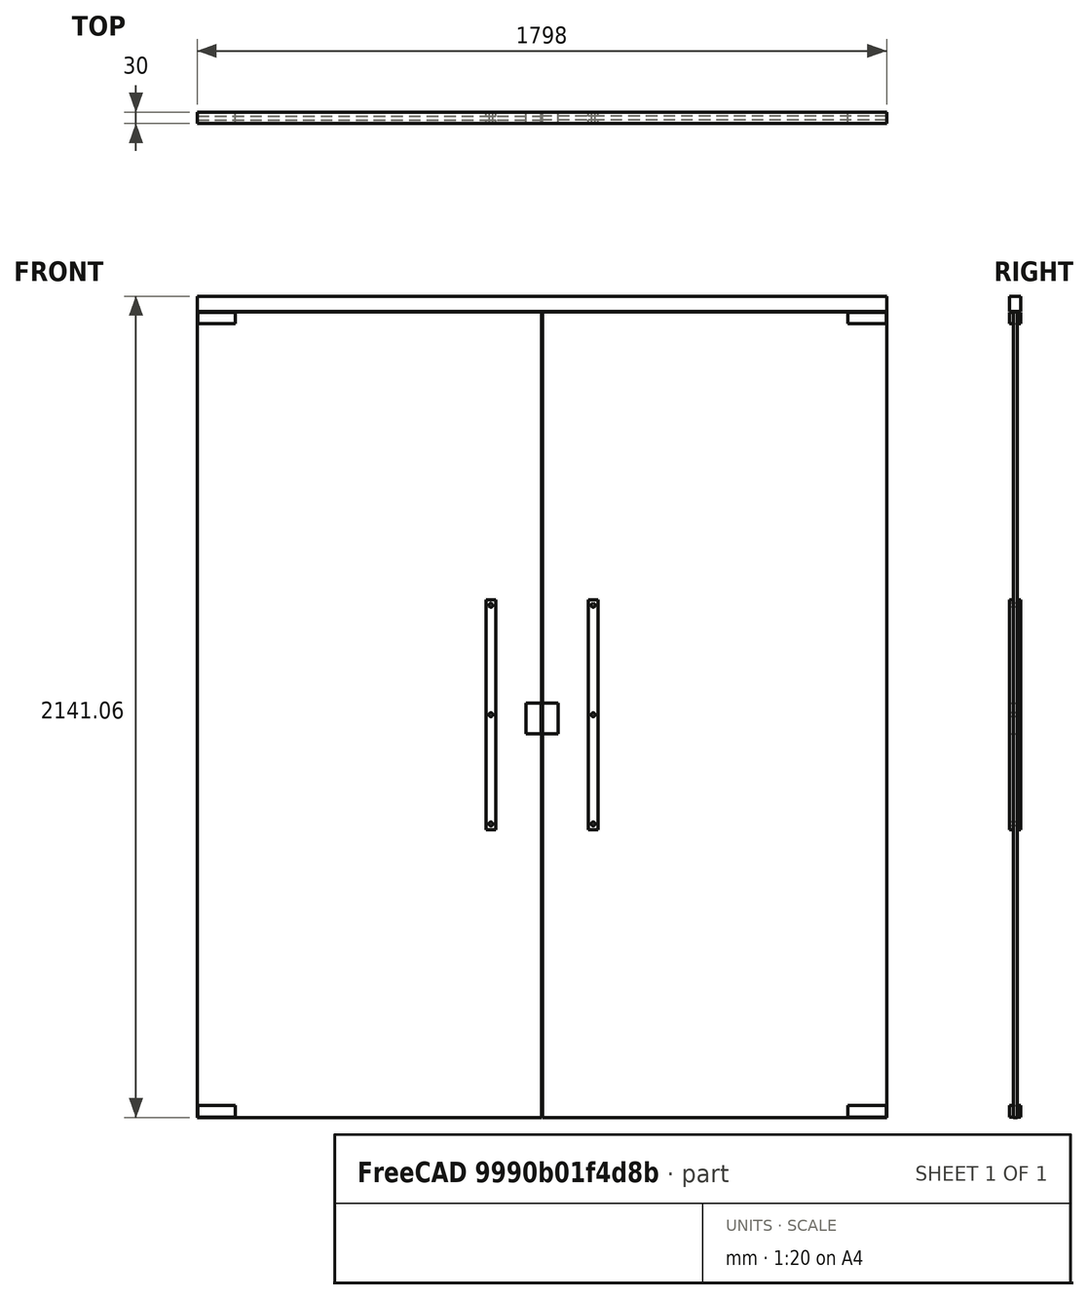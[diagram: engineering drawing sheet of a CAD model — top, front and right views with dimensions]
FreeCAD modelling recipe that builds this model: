
FCSTD DOCUMENT  (FreeCAD 0.16R6704 (Git))
Label: Double glass doors with lintel and handles
License: CreativeCommons Attribution
LicenseURL: http://creativecommons.org/licenses/by/4.0/
objects: Sketcher::SketchObject×3, Part::FeaturePython×1, App::DocumentObjectGroup×1
note: 4 computed .brp shape members not serialized (recipe doc carries the construction recipe); baked Part::Feature solids carry a one-line shape summary decoded from their .brp

FEATURE [Sketcher::SketchObject] Sketch135
  Placement = pos=(0,0,0) rot=(1,0,0;1.5708rad)
  sketch-geometry (63):
    g0: LineSegment StartX=0 StartY=0 StartZ=0 EndX=1800 EndY=0 EndZ=0
    g1: LineSegment StartX=1800 StartY=0 StartZ=0 EndX=1800 EndY=2142 EndZ=0
    g2: LineSegment StartX=1800 StartY=2142 StartZ=0 EndX=0 EndY=2142 EndZ=0
    g3: LineSegment StartX=0 StartY=2142 StartZ=0 EndX=0 EndY=0 EndZ=0
    g4: LineSegment StartX=1 StartY=0 StartZ=0 EndX=899 EndY=0 EndZ=0
    g5: LineSegment StartX=899 StartY=0 StartZ=0 EndX=899 EndY=2100 EndZ=0
    g6: LineSegment StartX=899 StartY=2100 StartZ=0 EndX=1 EndY=2100 EndZ=0
    g7: LineSegment StartX=1 StartY=2100 StartZ=0 EndX=1 EndY=0 EndZ=0
    g8: LineSegment StartX=2 StartY=2099 StartZ=0 EndX=100 EndY=2099 EndZ=0
    g9: LineSegment StartX=100 StartY=2099 StartZ=0 EndX=100 EndY=2069 EndZ=0
    g10: LineSegment StartX=100 StartY=2069 StartZ=0 EndX=2 EndY=2069 EndZ=0
    g11: LineSegment StartX=2 StartY=2069 StartZ=0 EndX=2 EndY=2099 EndZ=0
    g12: LineSegment StartX=2 StartY=1 StartZ=0 EndX=100 EndY=1 EndZ=0
    g13: LineSegment StartX=100 StartY=1 StartZ=0 EndX=100 EndY=31 EndZ=0
    g14: LineSegment StartX=100 StartY=31 StartZ=0 EndX=2 EndY=31 EndZ=0
    g15: LineSegment StartX=2 StartY=31 StartZ=0 EndX=2 EndY=1 EndZ=0
    g16: LineSegment StartX=858 StartY=1080 StartZ=0 EndX=898 EndY=1080 EndZ=0
    g17: LineSegment StartX=898 StartY=1080 StartZ=0 EndX=898 EndY=1000 EndZ=0
    g18: LineSegment StartX=898 StartY=1000 StartZ=0 EndX=858 EndY=1000 EndZ=0
    g19: LineSegment StartX=858 StartY=1000 StartZ=0 EndX=858 EndY=1080 EndZ=0
    g20: LineSegment StartX=754 StartY=1350 StartZ=0 EndX=779 EndY=1350 EndZ=0
    g21: LineSegment StartX=779 StartY=1350 StartZ=0 EndX=779 EndY=750 EndZ=0
    g22: LineSegment StartX=779 StartY=750 StartZ=0 EndX=754 EndY=750 EndZ=0
    g23: LineSegment StartX=754 StartY=750 StartZ=0 EndX=754 EndY=1350 EndZ=0
    g24: LineSegment [constr] StartX=766.5 StartY=1477.64 StartZ=0 EndX=766.5 EndY=711 EndZ=0
    g25: Circle CenterX=766.5 CenterY=1335 CenterZ=0 NormalX=0 NormalY=0 NormalZ=1 Radius=5
    g26: Circle CenterX=766.5 CenterY=1050 CenterZ=0 NormalX=0 NormalY=0 NormalZ=1 Radius=5
    g27: Circle CenterX=766.5 CenterY=765 CenterZ=0 NormalX=0 NormalY=0 NormalZ=1 Radius=5
    g28: LineSegment [constr] StartX=712 StartY=1050 StartZ=0 EndX=790 EndY=1050 EndZ=0
    g29: LineSegment [constr] StartX=900 StartY=2725.36 StartZ=0 EndX=900 EndY=-391.189 EndZ=0
    g30: LineSegment StartX=1799 StartY=-0.0580396 StartZ=0 EndX=901 EndY=-0.0580396 EndZ=0
    g31: LineSegment StartX=901 StartY=-0.0580396 StartZ=0 EndX=901 EndY=2100 EndZ=0
    g32: LineSegment StartX=901 StartY=2100 StartZ=0 EndX=1799 EndY=2100 EndZ=0
    g33: LineSegment StartX=1799 StartY=2100 StartZ=0 EndX=1799 EndY=-0.0580396 EndZ=0
    g34: LineSegment StartX=1798 StartY=2099 StartZ=0 EndX=1698 EndY=2099 EndZ=0
    g35: LineSegment StartX=1698 StartY=2099 StartZ=0 EndX=1698 EndY=2068.94 EndZ=0
    g36: LineSegment StartX=1698 StartY=2068.94 StartZ=0 EndX=1798 EndY=2068.94 EndZ=0
    g37: LineSegment StartX=1798 StartY=2068.94 StartZ=0 EndX=1798 EndY=2099 EndZ=0
    g38: LineSegment StartX=1798 StartY=0.94196 StartZ=0 EndX=1698 EndY=0.94196 EndZ=0
    g39: LineSegment StartX=1698 StartY=0.94196 StartZ=0 EndX=1698 EndY=31.0014 EndZ=0
    g40: LineSegment StartX=1698 StartY=31.0014 StartZ=0 EndX=1798 EndY=31.0014 EndZ=0
    g41: LineSegment StartX=1798 StartY=31.0014 StartZ=0 EndX=1798 EndY=0.94196 EndZ=0
    g42: LineSegment StartX=942 StartY=1080 StartZ=0 EndX=902 EndY=1080 EndZ=0
    g43: LineSegment StartX=902 StartY=1080 StartZ=0 EndX=902 EndY=1000 EndZ=0
    g44: LineSegment StartX=902 StartY=1000 StartZ=0 EndX=942 EndY=1000 EndZ=0
    g45: LineSegment StartX=942 StartY=1000 StartZ=0 EndX=942 EndY=1080 EndZ=0
    g46: LineSegment StartX=1046 StartY=1350 StartZ=0 EndX=1021 EndY=1350 EndZ=0
    g47: LineSegment StartX=1021 StartY=1350 StartZ=0 EndX=1021 EndY=750 EndZ=0
    g48: LineSegment StartX=1021 StartY=750 StartZ=0 EndX=1046 EndY=750 EndZ=0
    g49: LineSegment StartX=1046 StartY=750 StartZ=0 EndX=1046 EndY=1350 EndZ=0
    g50: LineSegment [constr] StartX=1033.5 StartY=1477.64 StartZ=0 EndX=1033.5 EndY=711 EndZ=0
    g51: Circle CenterX=1033.5 CenterY=1335 CenterZ=0 NormalX=0 NormalY=0 NormalZ=1 Radius=5
    g52: Circle CenterX=1033.5 CenterY=1050 CenterZ=0 NormalX=0 NormalY=0 NormalZ=1 Radius=5
    g53: Circle CenterX=1033.5 CenterY=765 CenterZ=0 NormalX=0 NormalY=0 NormalZ=1 Radius=5
    g54: LineSegment [constr] StartX=1088 StartY=1050 StartZ=0 EndX=1010 EndY=1050 EndZ=0
    g55: LineSegment StartX=-1 StartY=2143 StartZ=0 EndX=1801 EndY=2143 EndZ=0
    g56: LineSegment StartX=1801 StartY=2143 StartZ=0 EndX=1801 EndY=0 EndZ=0
    g57: LineSegment StartX=1801 StartY=0 StartZ=0 EndX=-1 EndY=0 EndZ=0
    g58: LineSegment StartX=-1 StartY=0 StartZ=0 EndX=-1 EndY=2143 EndZ=0
    g59: LineSegment StartX=1 StartY=2141 StartZ=0 EndX=1799 EndY=2141 EndZ=0
    g60: LineSegment StartX=1799 StartY=2141 StartZ=0 EndX=1799 EndY=2101 EndZ=0
    g61: LineSegment StartX=1799 StartY=2101 StartZ=0 EndX=1 EndY=2101 EndZ=0
    g62: LineSegment StartX=1 StartY=2101 StartZ=0 EndX=1 EndY=2141 EndZ=0
  constraints (177):
    c: Coincident(g0,g1)
    c: Coincident(g1,g2)
    c: Coincident(g2,g3)
    c: Coincident(g3,g0)
    c: Horizontal(g0)
    c: Horizontal(g2)
    c: Vertical(g1)
    c: Vertical(g3)
    c: Coincident(g4,g5)
    c: Coincident(g5,g6)
    c: Coincident(g6,g7)
    c: Coincident(g7,g4)
    c: Horizontal(g4)
    c: Horizontal(g6)
    c: Vertical(g5)
    c: Vertical(g7)
    c: DistanceX(g0) = 1800  'Largura vão'
    c: DistanceX(g2,g6) = 1  'Constraint18'
    c: DistanceY(g0,g4) = 0
    c: Coincident(g0,g-1)
    c: Coincident(g8,g9)
    c: Coincident(g9,g10)
    c: Coincident(g10,g11)
    c: Coincident(g11,g8)
    c: Horizontal(g8)
    c: Horizontal(g10)
    c: Vertical(g9)
    c: Vertical(g11)
    c: Coincident(g12,g13)
    c: Coincident(g13,g14)
    c: Coincident(g14,g15)
    c: Coincident(g15,g12)
    c: Horizontal(g12)
    c: Horizontal(g14)
    c: Vertical(g13)
    c: Vertical(g15)
    c: Coincident(g16,g17)
    c: Coincident(g17,g18)
    c: Coincident(g18,g19)
    c: Coincident(g19,g16)
    c: Horizontal(g16)
    c: Horizontal(g18)
    c: Vertical(g17)
    c: Vertical(g19)
    c: DistanceY(g8,g6) = 1
    c: DistanceX(g6,g8) = 1
    c: DistanceY(g9,g8) = 30  'Altura apoio'
    c: DistanceX(g10,g9) = 98  'Largura apoio'
    c: Equal(g9,g13)
    c: Equal(g14,g8)
    c: DistanceX(g4,g12) = 1
    c: DistanceY(g4,g12) = 1
    c: DistanceX(g17,g4) = 1
    c: DistanceY(g18,g16) = 80  'Altura tranca'
    c: DistanceX(g16,g16) = 40  'Largura tranca'
    c: DistanceY(g4,g18) = 1000  'Altura da tranca ao chão'
    c: Coincident(g20,g21)
    c: Coincident(g21,g22)
    c: Coincident(g22,g23)
    c: Coincident(g23,g20)
    c: Horizontal(g20)
    c: Horizontal(g22)
    c: Vertical(g21)
    c: Vertical(g23)
    c: DistanceX(g20,g20) = 25  'Largura puxador'
    c: DistanceY(g21,g20) = 600  'Altura do puxador'
    c: Vertical(g24)  'Constraint69'
    c: Symmetric(g20,g20,g24)
    c: PointOnObject(g25,g24)  'Constraint72'
    c: PointOnObject(g26,g24)  'Constraint71'
    c: PointOnObject(g27,g24)
    c: Radius(g27) = 5  'Apoio puxador'
    c: Equal(g27,g26)  'Constraint83'
    c: Equal(g27,g25)  'Constraint82'
    c: DistanceY(g25,g20) = 15
    c: DistanceY(g21,g27) = 15
    c: Horizontal(g28)
    c: PointOnObject(g26,g28)
    c: Symmetric(g22,g20,g28)
    c: DistanceY(g4,g21) = 750  'Distância do puxador ao solo'
    c: DistanceX(g21,g4) = 120  'Distância do puxador'
    c: Vertical(g29)
    c: Symmetric(g2,g1,g29)
    c: Coincident(g30,g31)
    c: Coincident(g31,g32)
    c: Coincident(g32,g33)
    c: Coincident(g33,g30)
    c: Horizontal(g30)
    c: Horizontal(g32)
    c: Vertical(g31)
    c: Vertical(g33)
    c: Coincident(g34,g35)
    c: Coincident(g35,g36)
    c: Coincident(g36,g37)
    c: Coincident(g37,g34)
    c: Horizontal(g34)
    c: Horizontal(g36)
    c: Vertical(g35)
    c: Vertical(g37)
    c: Coincident(g38,g39)
    c: Coincident(g39,g40)
    c: Coincident(g40,g41)
    c: Coincident(g41,g38)
    c: Horizontal(g38)
    c: Horizontal(g40)
    c: Vertical(g39)
    c: Vertical(g41)
    c: Coincident(g42,g43)
    c: Coincident(g43,g44)
    c: Coincident(g44,g45)
    c: Coincident(g45,g42)
    c: Horizontal(g42)
    c: Horizontal(g44)
    c: Vertical(g43)
    c: Vertical(g45)
    c: Equal(g35,g39)
    c: Equal(g40,g34)
    c: Coincident(g46,g47)
    c: Coincident(g47,g48)
    c: Coincident(g48,g49)
    c: Coincident(g49,g46)
    c: Horizontal(g46)
    c: Horizontal(g48)
    c: Vertical(g47)
    c: Vertical(g49)
    c: Vertical(g50)  'Constraint69'
    c: Symmetric(g46,g46,g50)
    c: PointOnObject(g51,g50)  'Constraint72'
    c: PointOnObject(g52,g50)
    c: PointOnObject(g53,g50)
    c: Radius(g53) = 5  'Apoio puxador'
    c: Equal(g53,g52)  'Constraint83'
    c: Equal(g53,g51)  'Constraint82'
    c: Horizontal(g54)
    c: PointOnObject(g52,g54)
    c: Symmetric(g48,g46,g54)
    c: Coincident(g55,g56)
    c: Coincident(g56,g57)
    c: Coincident(g57,g58)
    c: Coincident(g58,g55)
    c: Horizontal(g55)
    c: Horizontal(g57)
    c: Vertical(g56)
    c: Vertical(g58)
    c: DistanceX(g55,g2) = 1
    c: DistanceY(g2,g55) = 1
    c: DistanceX(g1,g55) = 1
    c: DistanceY(g57,g-1) = 0
    c: DistanceY(g-1,g6) = 2100  'Altura portas'
    c: Coincident(g59,g60)
    c: Coincident(g60,g61)
    c: Coincident(g61,g62)
    c: Coincident(g62,g59)
    c: Horizontal(g59)
    c: Horizontal(g61)
    c: Vertical(g60)
    c: Vertical(g62)
    c: DistanceX(g30,g0) = 1
    c: DistanceX(g60,g32) = 0
    c: DistanceX(g6,g61) = 0
    c: DistanceY(g6,g61) = 1
    c: DistanceY(g61,g59) = 40  'Altura perfil bandeira'
    c: DistanceY(g59,g2) = 1
    c: Symmetric(g16,g42,g29)
    c: DistanceX(g16,g42) = 4
    c: Equal(g16,g42)
    c: Equal(g19,g45)
    c: Symmetric(g24,g50,g29)
    c: DistanceY(g31,g5) = 0
    c: Symmetric(g5,g31,g29)
    c: DistanceX(g34,g32) = 1
    c: DistanceY(g34,g32) = 1
    c: DistanceX(g38,g30) = 1
    c: DistanceY(g30,g38) = 1
    c: Symmetric(g55,g55,g29)
    c: Equal(g20,g46)
    c: Equal(g21,g49)
FEATURE [Part::FeaturePython] Window095  label="Double glass doors with lintel and handles 001"  # WARN: FeaturePython — macro-defined, semantics opaque (R4)
  Base = -> Sketch135
  Height = 2100
  HoleDepth = 0
  MoveWithHost = true
  Normal = (0,1,0)
  Preset = 6
  Role = 1
  Width = 900
  WindowParts = PORTA 1 | Glass panel | Wire1 | 10.0 | 10.0 | APOIO SUPERIOR PORTA 1 | Frame | Wire2 | 30.0 | 0.0 | APOIO INFERIOR PORTA 1 | Frame | Wire3 | 30.0 | 0.0 | TRANCA 1 | Frame | Wire4 | 30.0 | 0.0 | PUXADOR 1A | Frame | Wire5 | 10.0 | 0.0 | PUXADOR 2A | Frame | Wire13 | 10.0 | 0.0 | APOIO SUPERIOR PUXADOR 1 | Frame | Wire6 | 30.0 | 0.0 | APOIO CENTRAL PUXADOR 1 | Frame | Wire7 | 30.0 | 0.0 | APOIO INFERIOR PUXADOR 1 | Frame | Wire8 | 30.0 | 0.0 | PORTA 2 | Glass panel | Wire9 | 10.0 | 10.0 | APOIOS SUPERIOR PORTA 2 | Frame | Wire10 | 30.0 | 0.0 | APOIO INFERIOR PORTA 2 | Frame | Wire11 | 30.0 | 0.0 | TRANCA 2 | Frame | Wire12 | 30.0 | 0.0 | APOIO SUPERIOR PUXADOR 2 | Frame | Wire14 | 30.0 | 0.0 | APOIO CENTRAL PUXADOR 2 | Frame | Wire15 | 30.0 | 0.0 | APOIO INFERIOR PUXADOR 2 | Frame | Wire16 | 30.0 | 0.0 | PUXADOR 2B | Frame | Wire13 | 10.0 | 20.0 | PERFIL BASE BANDEIRA | Frame | Wire18 | 30.0 | 0.0 | PUXADOR 1B | Frame | Wire5 | 10.0 | 20.0
FEATURE [Sketcher::SketchObject] Sketch136  label="Opening indication "
  ExternalGeometry = -> [Window095]
  Placement = pos=(0,10,0) rot=(1,0,0;1.5708rad)
  Support = -> Window095 [Face5]
  sketch-geometry (6):
    g0: LineSegment [constr] StartX=-578.323 StartY=1041.81 StartZ=0 EndX=1784.68 EndY=1041.81 EndZ=0
    g1: LineSegment [constr] StartX=60 StartY=2317.2 StartZ=0 EndX=60 EndY=-99.6345 EndZ=0
    g2: LineSegment StartX=1 StartY=1041.81 StartZ=0 EndX=60 EndY=2100 EndZ=0
    g3: LineSegment StartX=60 StartY=2100 StartZ=0 EndX=899 EndY=1041.81 EndZ=0
    g4: LineSegment StartX=899 StartY=1041.81 StartZ=0 EndX=60 EndY=0 EndZ=0
    g5: LineSegment StartX=60 StartY=0 StartZ=0 EndX=1 EndY=1041.81 EndZ=0
  constraints (16):
    c: Horizontal(g0)
    c: DistanceY(g-1,g0) = 1041.81  'Altura tranca'
    c: Vertical(g1)
    c: PointOnObject(g2,g0)
    c: Coincident(g2,g3)
    c: PointOnObject(g3,g-5)
    c: Coincident(g3,g4)
    c: PointOnObject(g4,g-6)
    c: Coincident(g4,g5)
    c: Coincident(g5,g2)
    c: PointOnObject(g2,g-4)
    c: PointOnObject(g2,g-3)
    c: PointOnObject(g2,g1)
    c: PointOnObject(g4,g1)
    c: PointOnObject(g3,g0)
    c: DistanceX(g-1,g1) = 60  'Eixo porta'
FEATURE [Sketcher::SketchObject] Sketch137  label="Opening indication 001"
  ExternalGeometry = -> [Window095]
  Placement = pos=(0,10,0) rot=(1,0,0;1.5708rad)
  Support = -> Window095 [Face50]
  sketch-geometry (6):
    g0: LineSegment [constr] StartX=-496.649 StartY=1041.19 StartZ=0 EndX=2033.7 EndY=1041.19 EndZ=0
    g1: LineSegment [constr] StartX=1739 StartY=2387.2 StartZ=0 EndX=1739 EndY=-146 EndZ=0
    g2: LineSegment StartX=899 StartY=1041.19 StartZ=0 EndX=1739 EndY=-0.0580396 EndZ=0
    g3: LineSegment StartX=1739 StartY=-0.0580396 StartZ=0 EndX=1799 EndY=1041.19 EndZ=0
    g4: LineSegment StartX=1799 StartY=1041.19 StartZ=0 EndX=1739 EndY=2100 EndZ=0
    g5: LineSegment StartX=1739 StartY=2100 StartZ=0 EndX=899 EndY=1041.19 EndZ=0
  constraints (16):
    c: Horizontal(g0)
    c: DistanceY(g-1,g0) = 1041.19  'Altura da tranca'
    c: Vertical(g1)
    c: DistanceX(g1,g-6) = 60  'Eixo porta'
    c: PointOnObject(g2,g-4)
    c: PointOnObject(g2,g-6)
    c: Coincident(g2,g3)
    c: PointOnObject(g3,g-5)
    c: Coincident(g3,g4)
    c: PointOnObject(g4,g-3)
    c: Coincident(g4,g5)
    c: Coincident(g5,g2)
    c: PointOnObject(g2,g0)
    c: PointOnObject(g3,g0)
    c: PointOnObject(g2,g1)
    c: PointOnObject(g4,g1)
FEATURE [App::DocumentObjectGroup] Grupo102  label="Double glass doors with lintel and handles "
  Group = -> [Window095,Sketch136,Sketch137]
